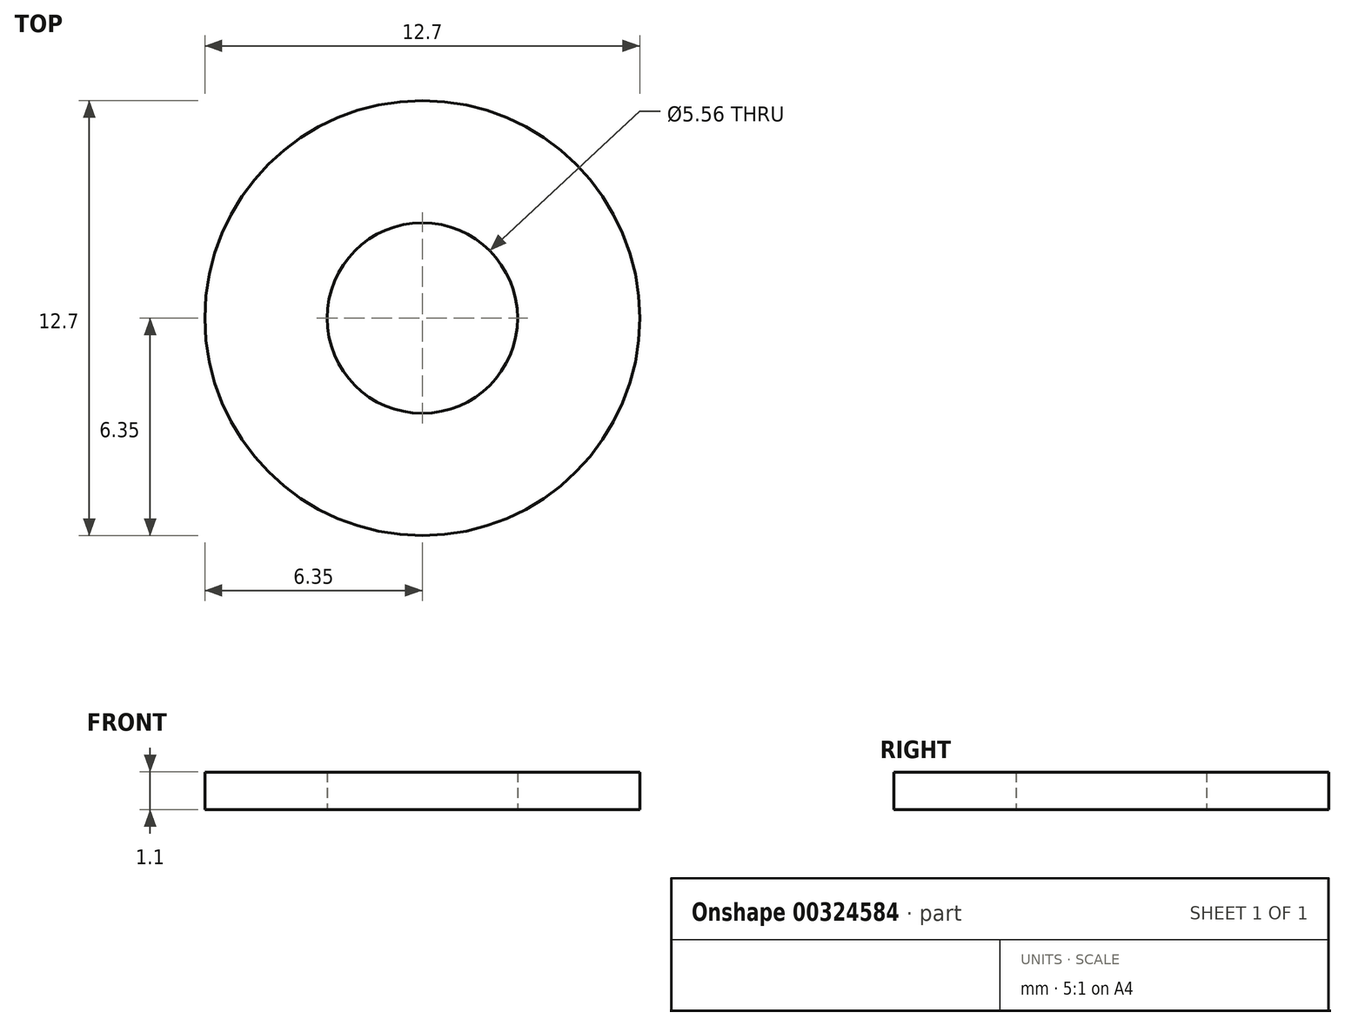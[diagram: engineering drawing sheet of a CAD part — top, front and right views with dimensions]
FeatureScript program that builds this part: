
annotation { "Feature Type Name" : "Feature", "Feature Type Description" : "" }
export const myFeature = defineFeature(function(context is Context, id is Id, definition is map)
    precondition{}
    {
        {
            var Q0;
            Q0=qCreatedBy(makeId("Top.planeOp"),FACE);
            var sketch = newSketch(context, id + "F0", { "sketchPlane" : qUnion([Q0])});
            skCircle(sketch, "E0", {"center": v(0, 0) * mm, "radius": 6.35 * mm});
            skCircle(sketch, "E1", {"center": v(0, 0) * mm, "radius": 2.78 * mm});
            skSolve(sketch);
        }
        {
            var Q0;
            Q0=makeQuery(id+"F0.imprint","IMPRINT",FACE,{"disambiguationData":[TD([[makeQuery(id+"F0.imprint","IMPRINT",EDGE,{"derivedFrom":sQuery(id+"F0.wireOp",EDGE,"E0")}),1.0]])]});
            extrude(context, id + "F1", {"entities" : qUnion([Q0]), "endBound" : BoundingType.SYMMETRIC, "depth" : 1.1 * mm});
        }
    });
